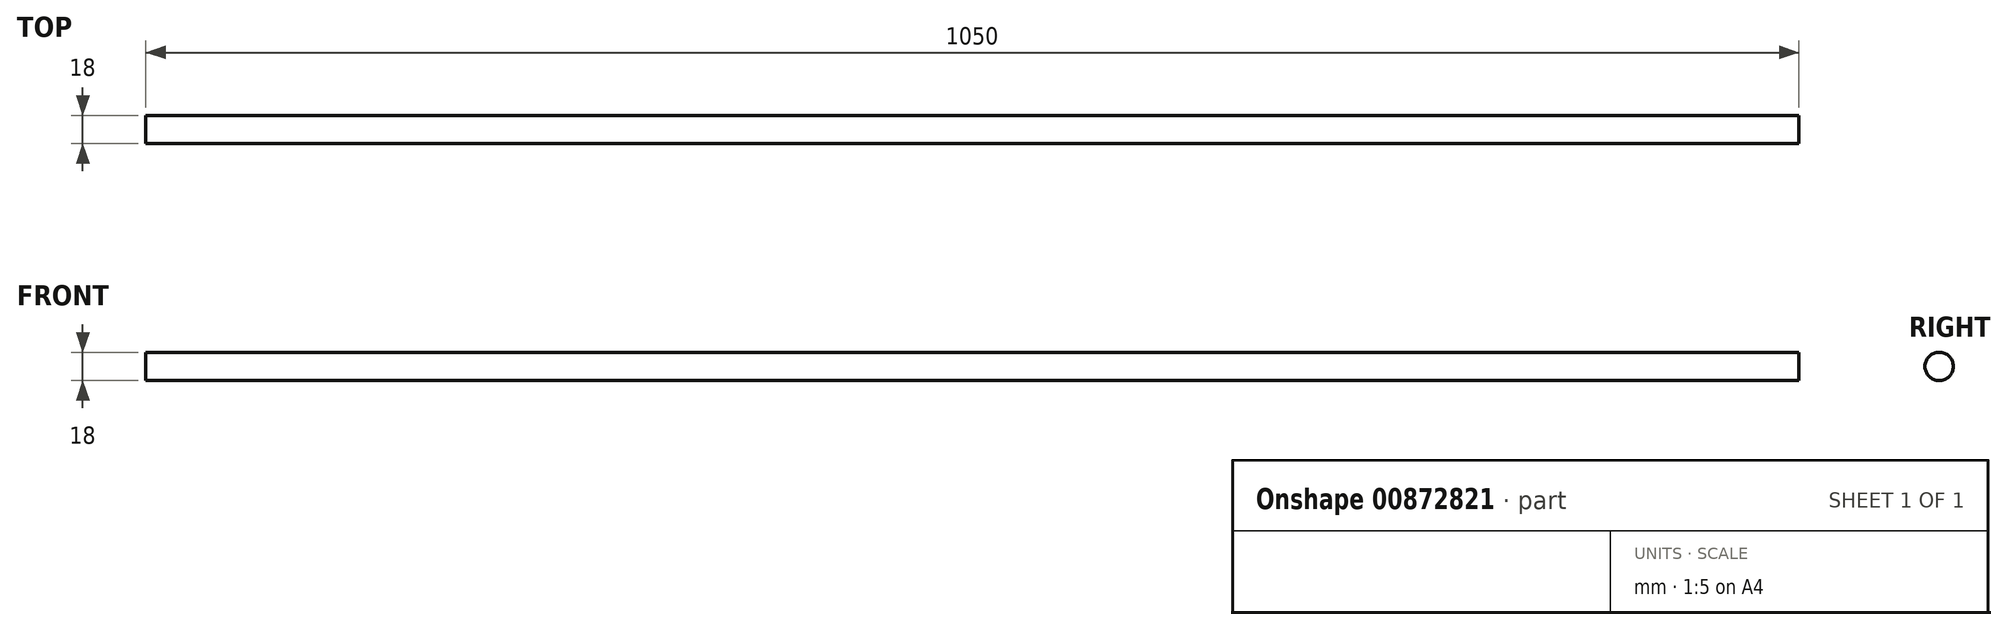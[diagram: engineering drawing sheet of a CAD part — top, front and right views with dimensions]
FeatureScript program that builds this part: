
annotation { "Feature Type Name" : "Feature", "Feature Type Description" : "" }
export const myFeature = defineFeature(function(context is Context, id is Id, definition is map)
    precondition{}
    {
        {
            var Q0;
            Q0=qCreatedBy(makeId("Right.planeOp"),FACE);
            var sketch = newSketch(context, id + "F0", { "sketchPlane" : qUnion([Q0])});
            skCircle(sketch, "E0", {"center": v(0, 0) * mm, "radius": 9 * mm});
            skSolve(sketch);
        }
        {
            var Q0;
            Q0 = qSketchRegion(id + "F0", true);
            extrude(context, id + "F1", {"entities" : qUnion([Q0]), "depth" : 1050 * mm, "offsetDistance" : 25 * mm});
        }
    });
